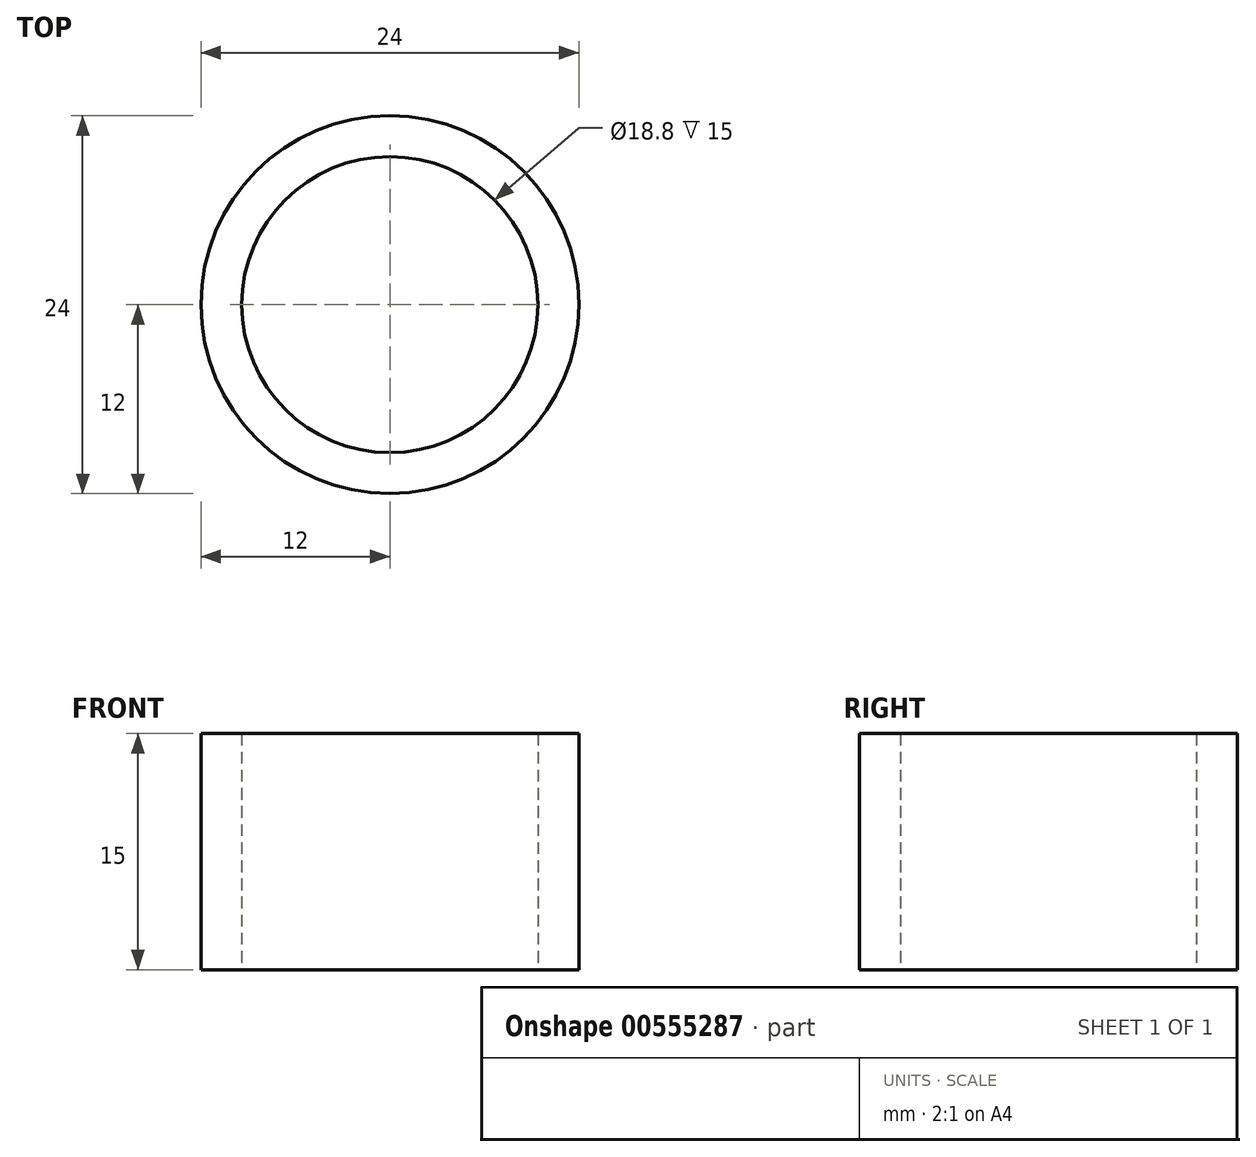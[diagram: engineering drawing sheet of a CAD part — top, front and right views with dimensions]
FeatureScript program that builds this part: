
annotation { "Feature Type Name" : "Feature", "Feature Type Description" : "" }
export const myFeature = defineFeature(function(context is Context, id is Id, definition is map)
    precondition{}
    {
        {
            var Q0;
            Q0=qCreatedBy(makeId("Top.planeOp"),FACE);
            var sketch = newSketch(context, id + "F0", { "sketchPlane" : qUnion([Q0])});
            skCircle(sketch, "E0", {"center": v(0, 0) * mm, "radius": 9.4 * mm});
            skCircle(sketch, "E1", {"center": v(0, 0) * mm, "radius": 12 * mm});
            skSolve(sketch);
        }
        {
            var Q0;
            Q0 = qSketchRegion(id + "F0", true);
            extrude(context, id + "F1", {"entities" : qUnion([Q0]), "depth" : 15 * mm, "offsetDistance" : 25 * mm});
        }
    });
